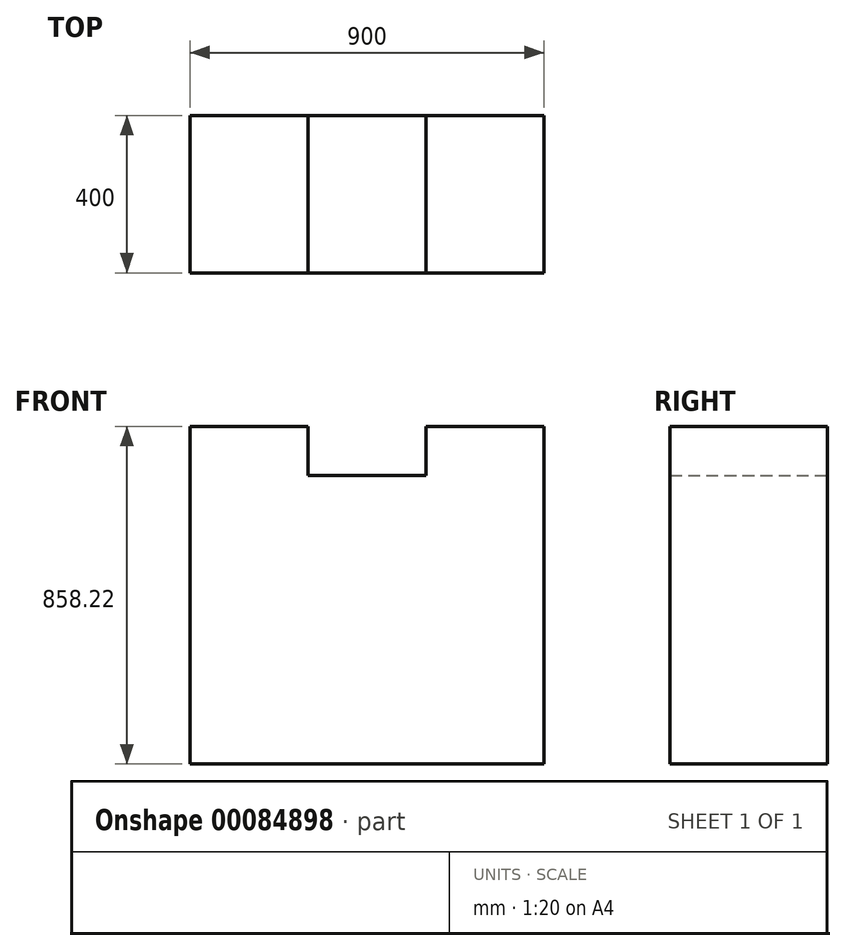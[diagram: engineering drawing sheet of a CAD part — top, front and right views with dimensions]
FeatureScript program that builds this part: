
annotation { "Feature Type Name" : "Feature", "Feature Type Description" : "" }
export const myFeature = defineFeature(function(context is Context, id is Id, definition is map)
    precondition{}
    {
        {
            var Q0;
            Q0=qCreatedBy(makeId("Front.planeOp"),FACE);
            var sketch = newSketch(context, id + "F0", { "sketchPlane" : qUnion([Q0])});
            skLineSegment(sketch, "E0.bottom", {"start": v(-450, -429.11) * mm, "end": v(450, -429.11) * mm});
            skLineSegment(sketch, "E0.top", {"start": v(-450, 429.11) * mm, "end": v(-150, 429.11) * mm});
            skLineSegment(sketch, "E0.left", {"start": v(-450, -429.11) * mm, "end": v(-450, 429.11) * mm});
            skLineSegment(sketch, "E0.right", {"start": v(450, -429.11) * mm, "end": v(450, 429.11) * mm});
            skPoint(sketch, "E0.middle", {"position": v(0, 0) * mm});
            skLineSegment(sketch, "E1.bottom", {"start": v(-150, 304.11) * mm, "end": v(150, 304.11) * mm});
            skLineSegment(sketch, "E1.left", {"start": v(-150, 304.11) * mm, "end": v(-150, 429.11) * mm});
            skLineSegment(sketch, "E1.right", {"start": v(150, 304.11) * mm, "end": v(150, 429.11) * mm});
            skPoint(sketch, "E1.middle", {"position": v(0, 429.11) * mm});
            skLineSegment(sketch, "E2.trimOffspring", {"start": v(150, 429.11) * mm, "end": v(450, 429.11) * mm});
            skPoint(sketch, "E1.top.end.orphan", {"position": v(150, 554.11) * mm});
            skPoint(sketch, "E3.orphan", {"position": v(-150, 554.11) * mm});
            skSolve(sketch);
        }
        {
            var Q0;
            Q0 = qSketchRegion(id + "F0", true);
            extrude(context, id + "F1", {"entities" : qUnion([Q0]), "depth" : 400 * mm});
        }
    });
